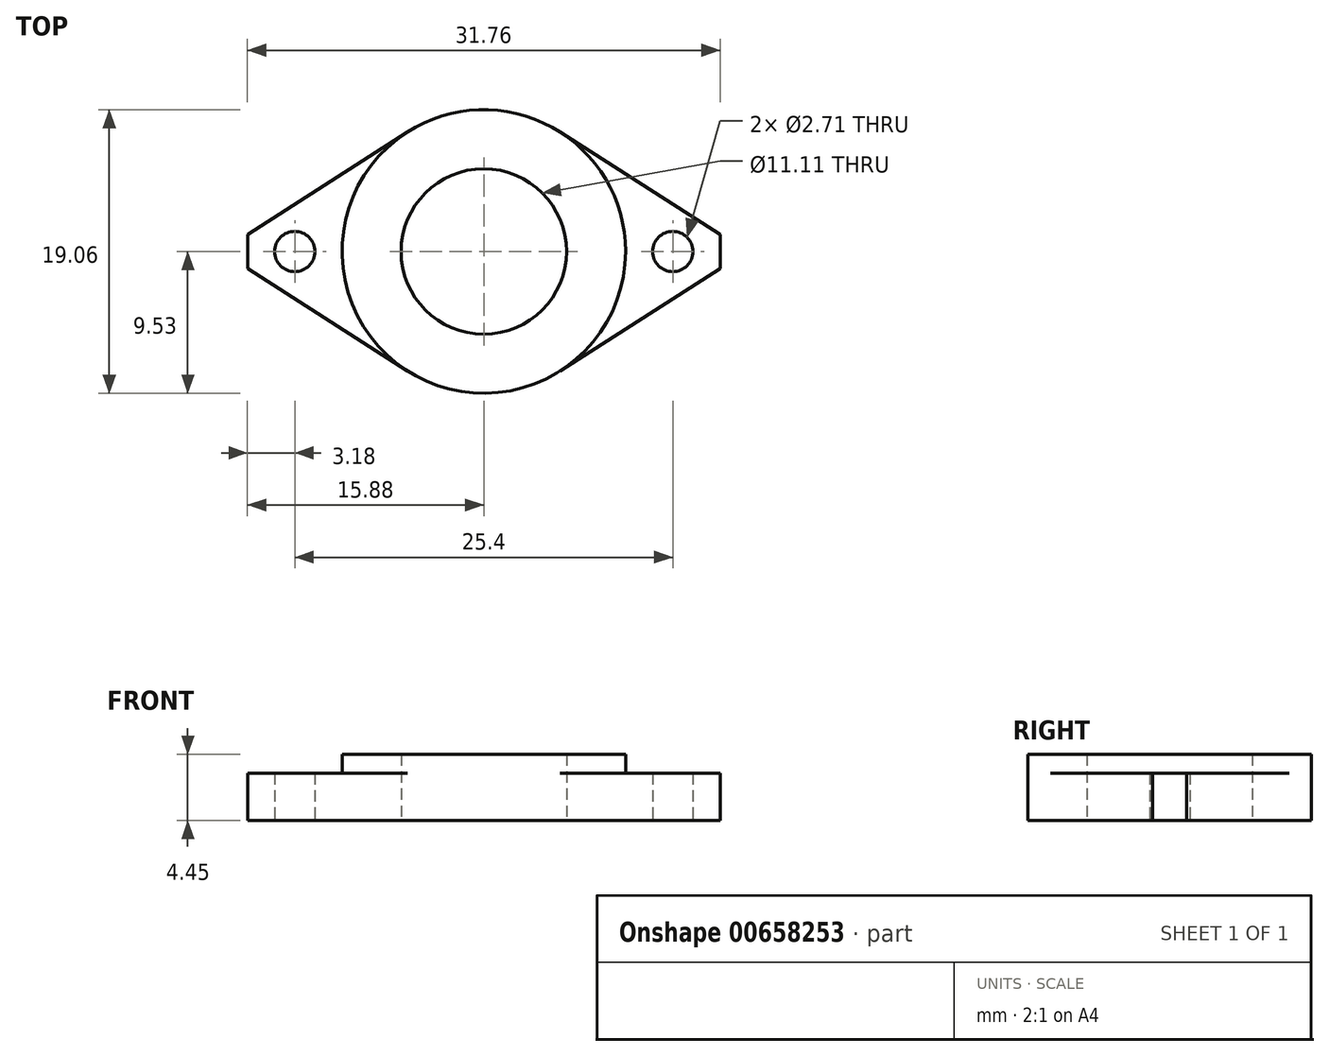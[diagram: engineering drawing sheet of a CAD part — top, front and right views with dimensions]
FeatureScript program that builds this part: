
annotation { "Feature Type Name" : "Feature", "Feature Type Description" : "" }
export const myFeature = defineFeature(function(context is Context, id is Id, definition is map)
    precondition{}
    {
        {
            var Q0;
            Q0=qCreatedBy(makeId("Top.planeOp"),FACE);
            var sketch = newSketch(context, id + "F0", { "sketchPlane" : qUnion([Q0])});
            skCircle(sketch, "E0", {"center": v(0, 0) * mm, "radius": 9.53 * mm});
            skCircle(sketch, "E1", {"center": v(0, 0) * mm, "radius": 5.56 * mm});
            skSolve(sketch);
        }
        {
            var Q0;
            Q0=makeQuery(id+"F0.imprint","IMPRINT",FACE,{"disambiguationData":[TD([[makeQuery(id+"F0.imprint","IMPRINT",EDGE,{"derivedFrom":sQuery(id+"F0.wireOp",EDGE,"E0")}),1.0]])]});
            extrude(context, id + "F1", {"entities" : qUnion([Q0]), "depth" : 4.44 * mm, "offsetDistance" : 25.4 * mm});
        }
        {
            var Q0;
            Q0=makeQuery(id+"F1.opExtrude","CAP_FACE",FACE,{"disambiguationData":[OSD([sQuery(id+"F0.wireOp",EDGE,"E0"),sQuery(id+"F0.wireOp",EDGE,"E1")])],"isStart":true});
            var sketch = newSketch(context, id + "F2", { "sketchPlane" : qUnion([Q0])});
            skLineSegment(sketch, "E2", {"start": v(0, 0) * mm, "end": v(-12.7, 0) * mm, "construction": true});
            skCircle(sketch, "E3", {"center": v(-12.7, 0) * mm, "radius": 1.35 * mm});
            skPoint(sketch, "E4", {"position": v(-9.53, 0) * mm});
            skLineSegment(sketch, "E5", {"start": v(-12.7, 0) * mm, "end": v(-12.7, 3.18) * mm, "construction": true});
            skLineSegment(sketch, "E6", {"start": v(-12.7, 3.17) * mm, "end": v(-12.7, 0) * mm, "construction": true});
            skLineSegment(sketch, "E7", {"start": v(-12.7, -3.17) * mm, "end": v(-12.7, 0) * mm, "construction": true});
            skPoint(sketch, "E8", {"position": v(-12.7, 3.18) * mm});
            skPoint(sketch, "E9", {"position": v(-12.7, -3.18) * mm});
            skLineSegment(sketch, "E10", {"start": v(-12.7, 3.18) * mm, "end": v(-5.14, 8.02) * mm});
            skLineSegment(sketch, "E11", {"start": v(-12.7, -3.18) * mm, "end": v(-5.14, -8.02) * mm});
            skLineSegment(sketch, "E12", {"start": v(-12.7, 3.17) * mm, "end": v(-15.88, 1.14) * mm});
            skLineSegment(sketch, "E13", {"start": v(-15.88, -1.14) * mm, "end": v(-12.7, -3.17) * mm});
            skPoint(sketch, "E14", {"position": v(-15.88, 0) * mm});
            skLineSegment(sketch, "E15", {"start": v(-15.88, 1.14) * mm, "end": v(-15.88, -1.14) * mm});
            skLineSegment(sketch, "E16", {"start": v(0, 0) * mm, "end": v(24.46, 0) * mm, "construction": true});
            skPoint(sketch, "E17", {"position": v(12.7, 0) * mm});
            skPoint(sketch, "E18", {"position": v(9.53, 0) * mm});
            skCircle(sketch, "E19", {"center": v(12.7, 0) * mm, "radius": 1.35 * mm});
            skPoint(sketch, "E20", {"position": v(15.88, 0) * mm});
            skLineSegment(sketch, "E21", {"start": v(15.88, 1.14) * mm, "end": v(15.88, -1.14) * mm});
            skLineSegment(sketch, "E22", {"start": v(15.88, -1.14) * mm, "end": v(5.14, -8.02) * mm});
            skLineSegment(sketch, "E23", {"start": v(15.88, 1.14) * mm, "end": v(5.14, 8.02) * mm});
            skSolve(sketch);
        }
        {
            var Q0;
            Q0=makeQuery(id+"F2.imprint","IMPRINT",FACE,{"disambiguationData":[TD([[makeQuery(id+"F2.imprint","IMPRINT",EDGE,{"derivedFrom":sQuery(id+"F2.wireOp",EDGE,"E3")}),-1.0]])]});
            var Q1;
            Q1=makeQuery(id+"F2.imprint","IMPRINT",FACE,{"disambiguationData":[TD([[makeQuery(id+"F2.imprint","IMPRINT",EDGE,{"derivedFrom":sQuery(id+"F2.wireOp",EDGE,"E19")}),-1.0]])]});
            extrude(context, id + "F3", {"entities" : qUnion([Q0, Q1]), "operationType" : NewBodyOperationType.ADD, "oppositeDirection" : true, "depth" : 3.17 * mm, "offsetDistance" : 25.4 * mm});
        }
    });
